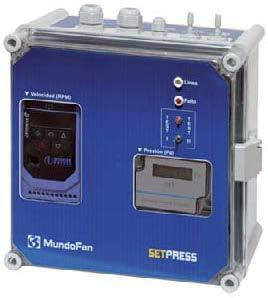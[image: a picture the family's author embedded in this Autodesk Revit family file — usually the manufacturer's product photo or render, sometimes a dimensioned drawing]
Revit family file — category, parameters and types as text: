
# Revit family: SETPRESS-55_VE10811
name_source: partatom
category: Aparatos eléctricos
revit_build: Autodesk Revit 2016 (Build: 20150220_1215(x64)
units: mm (PartAtom-declared; Revit-internal decimal feet)

## family parameters
Compartido = No
Corte con vacíos al cargar = No
Cota de conector redondo = Diámetro de uso
Mantener orientación de anotación = No
Número OmniClass = 23.80.00.00
Punto de cálculo de habitación = No
Se basa en plano de trabajo = No
Siempre vertical = Sí
Tipo de pieza = Caja de conexiones
Título OmniClass = Electric Power and Lighting

## types (1)
- SETPRESS
    Alimentación = 400Vac trifásico
    Corriente = 14 A
    Costo = 0 $
    Código de montaje = VE10811
    Descripción = CONTROL EFICIENCIA ENERGETICA PARA VENTILADORES
    Dimensiones máx. = 270x300x170 mm
    Fabricante = SALVADOR ESCODA
    Imagen de tipo = setpress.jpg
    Leds = linea / fallo
    Modelo = SETPRESS 5,5 kW
    Normativas = UNE-EN 12101-6
    Potencia = 5,5 kW
    Regulación = Mediante sonda analógica de presión
    Salida = 400Vac trifásico
    URL = www.salvadorescoda.com
    Visualización = frecuencia (Hz) y presión (Pa)
